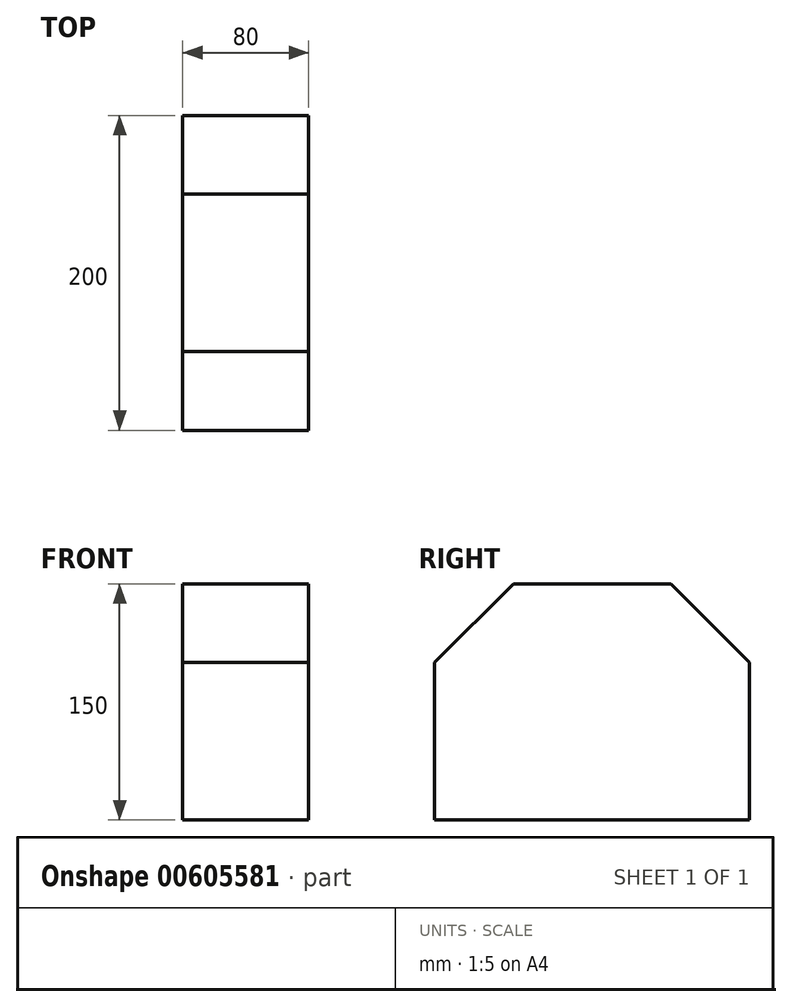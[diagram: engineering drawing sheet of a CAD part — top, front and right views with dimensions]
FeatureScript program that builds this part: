
annotation { "Feature Type Name" : "Feature", "Feature Type Description" : "" }
export const myFeature = defineFeature(function(context is Context, id is Id, definition is map)
    precondition{}
    {
        {
            var Q0;
            Q0=qCreatedBy(makeId("Top.planeOp"),FACE);
            var sketch = newSketch(context, id + "F0", { "sketchPlane" : qUnion([Q0])});
            skLineSegment(sketch, "E0.bottom", {"start": v(0, 0) * mm, "end": v(80, 0) * mm});
            skLineSegment(sketch, "E0.top", {"start": v(0, -200) * mm, "end": v(80, -200) * mm});
            skLineSegment(sketch, "E0.left", {"start": v(0, 0) * mm, "end": v(0, -200) * mm});
            skLineSegment(sketch, "E0.right", {"start": v(80, 0) * mm, "end": v(80, -200) * mm});
            skSolve(sketch);
        }
        {
            var Q0;
            Q0=makeQuery(id+"F0.imprint","IMPRINT",FACE,{"disambiguationData":[TD([[makeQuery(id+"F0.imprint","IMPRINT",EDGE,{"derivedFrom":sQuery(id+"F0.wireOp",EDGE,"E0.bottom")}),-1.0]])]});
            extrude(context, id + "F1", {"entities" : qUnion([Q0]), "depth" : 150 * mm, "offsetDistance" : 25.4 * mm});
        }
        {
            var Q0;
            Q0=makeQuery(id+"F1.opExtrude","CAP_EDGE",EDGE,{"disambiguationData":[OSD([sQuery(id+"F0.wireOp",EDGE,"E0.bottom")])],"isStart":false});
            var Q1;
            Q1=makeQuery(id+"F1.opExtrude","CAP_EDGE",EDGE,{"disambiguationData":[OSD([sQuery(id+"F0.wireOp",EDGE,"E0.top")])],"isStart":false});
            chamfer(context, id + "F2", {"entities" : qUnion([Q0, Q1]), "width" : 50 * mm, "tangentPropagation" : true});
        }
    });
